# Revit family: Haworth_BeHold_Modular_MobileCredenza
name_source: partatom
category: Furniture Systems
revit_build: Autodesk Revit 2018 (Build: 20170223_1515(x64)
units: mm (PartAtom-declared; Revit-internal decimal feet)

## family parameters
Always vertical = Yes
Cut with Voids When Loaded = No
OmniClass Number = 23.40.70.14.64.21
OmniClass Title = Systems Furniture
Part Type = Normal
Room Calculation Point = No
Round Connector Dimension = Use Diameter
Shared = No
Work Plane-Based = No

## types (2) — shared parameters
Actual Depth = 16"
Actual Height = 22"
Actual Storage Width = 24"
Actual Width = 48"
Assembly Code = E2020200
Back Caster Offset = 1 3/16"
Blade Pull = Yes
Blade Pull Length = 23 13/16"
Bottom Case Offset = 1 3/4"
Bottom Drawer Height = 12 3/4"
Bottom Drawer Offset = 2 5/8"
Case Thickness = 3/4"
Caster Finish = Haworth _ Polymer _ Slate
Classic Pull = No
Classic Pull Length = 6 3/4"
Cresent Pull = No
Description = Haworth - Be_Hold - Modular Mobile Credenza
Distance Between Drawer = 1/8"
Drawer Width = 23 7/8"
Front Caster Offset = 1 7/8"
Linear Pull = No
Linear Pull Length = 8"
Manufacturer = Haworth
Max. Depth = 16"
Max. Height = 22"
Max. Width = 72"
Min. Depth = 16"
Min. Height = 22"
Min. Width = 72"
Model = Haworth Be_Hold
Revision Number = 1
Shelf 1 Offset = 12 15/16"
Side Case Front Offset = 3/4"
Side Caster Offset = 1 9/16"
Size = Verify Final Dim. w/ Haworth
Sustainability Info = https://www.haworth.com
Top Case Front Offset = 3"
Top Drawer Height = 6 3/8"
Top Thickness = 3/4"
Total Drawer Height = 19 1/4"
URL = www.haworth.com
URL - Product = http://www.haworth.com
Warranty = http://www.haworth.com
Wing Pull = No
Wing Pull Length = 16 3/4"
With Lock = Yes

## per-type parameters (varying)
| type | Back Case Back Control | Back Case Side Control | Inset Style | Proud Style | Side Case Back Control | Top Case Back Control |
| Proud Back | 0" | 0" | No | Yes | 3/4" | 0" |
| Inset Back | 3/16" | 3/4" | Yes | No | 0" | 3/16" |

## geometry (parser evidence)
native form markers: Sweep x7
no freeform markers — native parametric forms only
